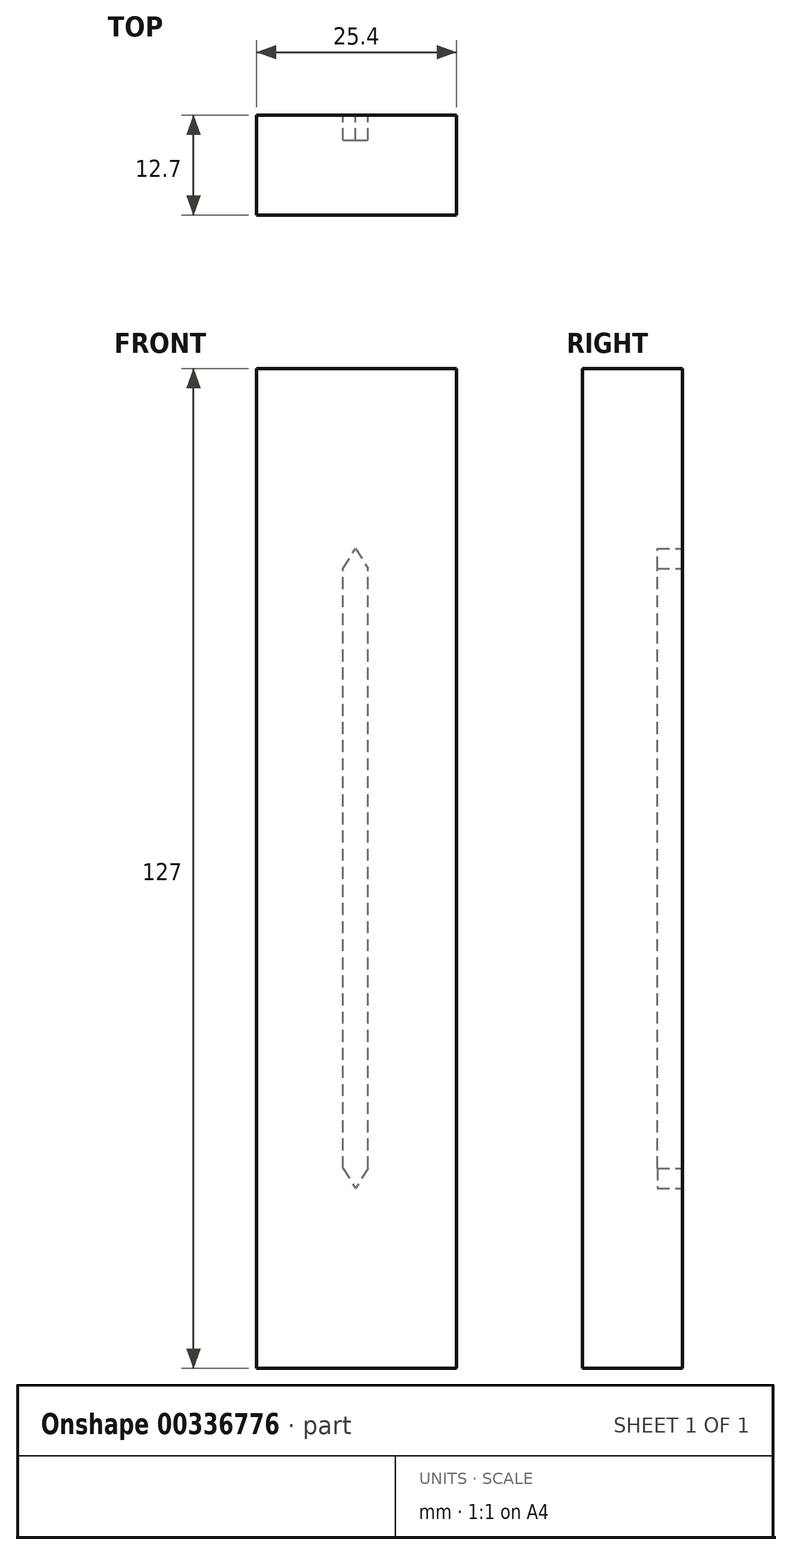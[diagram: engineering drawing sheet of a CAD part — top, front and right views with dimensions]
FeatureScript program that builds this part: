
annotation { "Feature Type Name" : "Feature", "Feature Type Description" : "" }
export const myFeature = defineFeature(function(context is Context, id is Id, definition is map)
    precondition{}
    {
        {
            var Q0;
            Q0=qCreatedBy(makeId("Top.planeOp"),FACE);
            var sketch = newSketch(context, id + "F0", { "sketchPlane" : qUnion([Q0])});
            skLineSegment(sketch, "E0.bottom", {"start": v(0, 0) * mm, "end": v(25.4, 0) * mm});
            skLineSegment(sketch, "E0.top", {"start": v(0, 12.7) * mm, "end": v(25.4, 12.7) * mm});
            skLineSegment(sketch, "E0.left", {"start": v(0, 0) * mm, "end": v(0, 12.7) * mm});
            skLineSegment(sketch, "E0.right", {"start": v(25.4, 0) * mm, "end": v(25.4, 12.7) * mm});
            skSolve(sketch);
        }
        {
            var Q0;
            Q0=makeQuery(id+"F0.imprint","IMPRINT",FACE,{"disambiguationData":[TD([[makeQuery(id+"F0.imprint","IMPRINT",EDGE,{"derivedFrom":sQuery(id+"F0.wireOp",EDGE,"E0.bottom")}),1.0]])]});
            extrude(context, id + "F1", {"entities" : qUnion([Q0]), "depth" : 127 * mm});
        }
        {
            var Q0;
            Q0=makeQuery(id+"F1.opExtrude","SWEPT_FACE",FACE,{"disambiguationData":[OSD([sQuery(id+"F0.wireOp",EDGE,"E0.top")])]});
            var sketch = newSketch(context, id + "F2", { "sketchPlane" : qUnion([Q0])});
            skLineSegment(sketch, "E1.left", {"start": v(-10.98, 25.4) * mm, "end": v(-10.98, 101.6) * mm});
            skLineSegment(sketch, "E1.right", {"start": v(-14.16, 25.4) * mm, "end": v(-14.16, 101.6) * mm});
            skPoint(sketch, "E2", {"position": v(-12.57, 22.86) * mm});
            skLineSegment(sketch, "E3", {"start": v(-10.98, 25.4) * mm, "end": v(-12.57, 22.86) * mm});
            skLineSegment(sketch, "E4", {"start": v(-14.16, 25.4) * mm, "end": v(-12.57, 22.86) * mm});
            skPoint(sketch, "E5", {"position": v(-12.57, 104.14) * mm});
            skLineSegment(sketch, "E6", {"start": v(-10.98, 101.6) * mm, "end": v(-12.57, 104.14) * mm});
            skLineSegment(sketch, "E7", {"start": v(-12.57, 104.14) * mm, "end": v(-14.16, 101.6) * mm});
            skSolve(sketch);
        }
        {
            var Q0;
            Q0=makeQuery(id+"F2.imprint","IMPRINT",FACE,{"disambiguationData":[TD([[makeQuery(id+"F2.imprint","IMPRINT",EDGE,{"derivedFrom":sQuery(id+"F2.wireOp",EDGE,"E1.left")}),1.0]])]});
            extrude(context, id + "F3", {"entities" : qUnion([Q0]), "operationType" : NewBodyOperationType.REMOVE, "oppositeDirection" : true, "depth" : 3.17 * mm});
        }
    });
